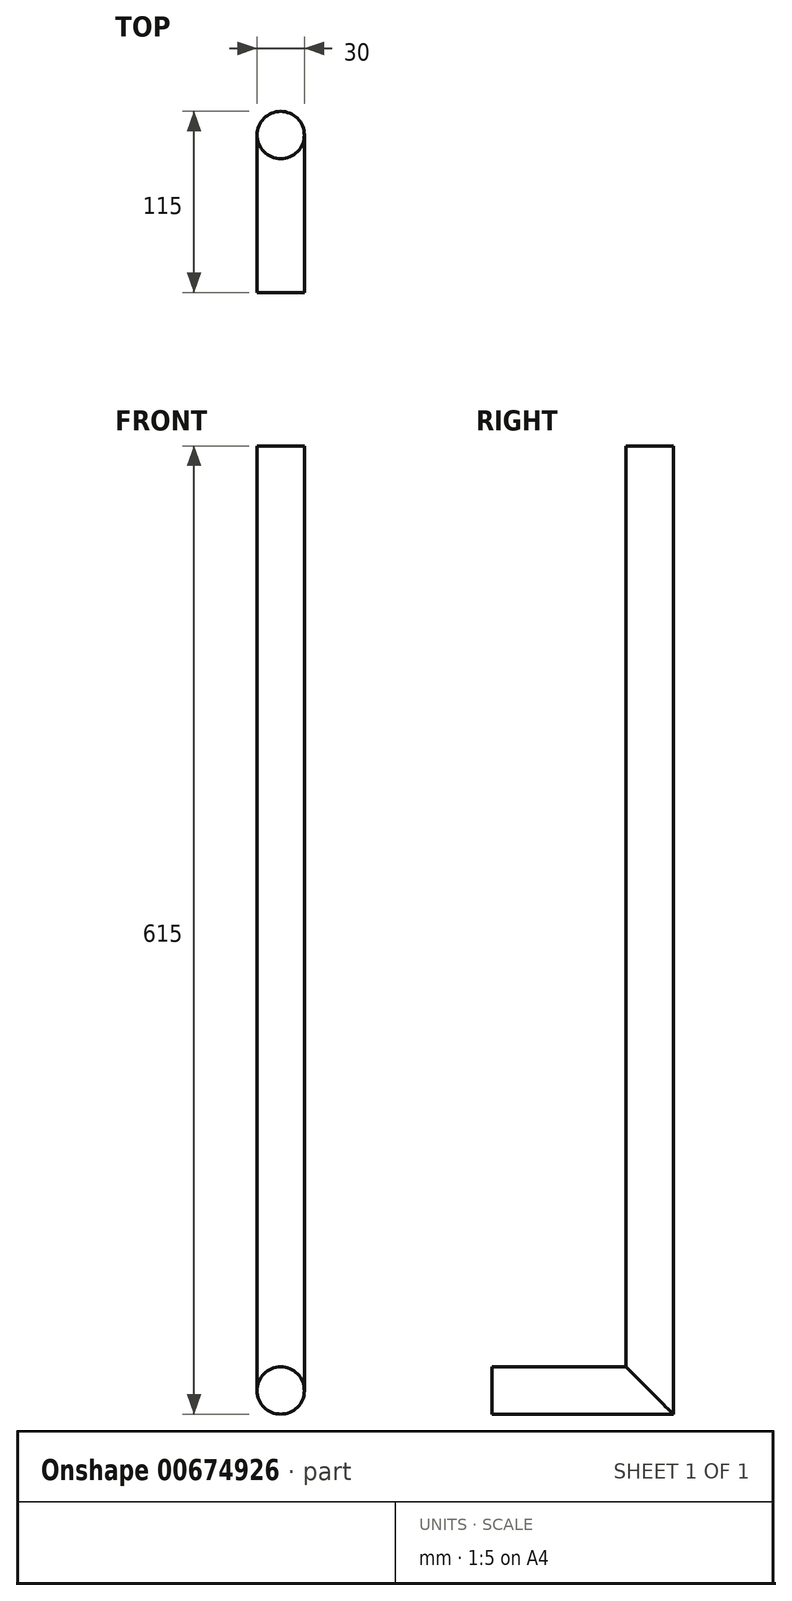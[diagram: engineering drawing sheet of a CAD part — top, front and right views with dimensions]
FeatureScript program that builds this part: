
annotation { "Feature Type Name" : "Feature", "Feature Type Description" : "" }
export const myFeature = defineFeature(function(context is Context, id is Id, definition is map)
    precondition{}
    {
        {
            var Q0;
            Q0=qCreatedBy(makeId("Front.planeOp"),FACE);
            var sketch = newSketch(context, id + "F0", { "sketchPlane" : qUnion([Q0])});
            skCircle(sketch, "E0", {"center": v(0, 0) * mm, "radius": 15 * mm});
            skSolve(sketch);
        }
        {
            var Q0;
            Q0=qCreatedBy(makeId("Right.planeOp"),FACE);
            var sketch = newSketch(context, id + "F1", { "sketchPlane" : qUnion([Q0])});
            skLineSegment(sketch, "E1", {"start": v(0, 0) * mm, "end": v(100, 0) * mm});
            skLineSegment(sketch, "E2", {"start": v(100, 0) * mm, "end": v(100, 600) * mm});
            skSolve(sketch);
        }
        {
            var Q0;
            Q0=makeQuery(id+"F0.imprint","IMPRINT",FACE,{"disambiguationData":[TD([[makeQuery(id+"F0.imprint","IMPRINT",EDGE,{"derivedFrom":sQuery(id+"F0.wireOp",EDGE,"E0")}),1.0]])]});
            var Q1;
            Q1=sQuery(id+"F1.wireOp",EDGE,"E1");
            var Q2;
            Q2=sQuery(id+"F1.wireOp",EDGE,"E2");
            sweep(context, id + "F2", {"profiles" : qUnion([Q0]), "path" : qUnion([Q1, Q2])});
        }
    });
